# Revit family: BuroSeating_Konfurb Orbit MB_Pedestal
name_source: partatom
category: Furniture
units: mm (PartAtom-declared; Revit-internal decimal feet)

## family parameters
Always vertical = Yes
Cut with Voids When Loaded = No
OmniClass Number = 23.40.70.14.64.11
OmniClass Title = Office Furniture
Room Calculation Point = No
Shared = Yes
Work Plane-Based = No

## types (2) — shared parameters
Assembly Code = E2020
Description = Konfurb Orbi Pedestal Mid Back
Manufacturer = Buro Seating
Model = KON185
NominalDepth = 600 mm
NominalHeight = 835 mm
NominalWidth = 650 mm  [stored 2.13255 ft]
ProductGroup = Orbit
ProductPageURL AU = https://buroseating.com
ProductPageURL NZ = https://buroseating.co.nz
ProductRange = Konfurb
SeatArms = No
SeatBackHeght = 360 mm  [stored 1.1811 ft]
SeatDepth = 470 mm  [stored 1.54199 ft]
SeatHeadRest = No
SeatHeight = 400 mm  [stored 1.31234 ft]
SeatWidth = 515 mm  [stored 1.68963 ft]
Type Comments = Seat Height 435 High
URL = https://buroseating.co.nz
URL AU = https://buroseating.com
WarrantyDescription = Full 5 year guarantee (excluding upholstery)
zero-valued in all types: Default Elevation

## per-type parameters (varying)
| type | BaseFrameMaterial | FeetMaterial | FrameMaterial |
| Buro Elan 159-M3 | <By Category> | <By Category> | <By Category> |
| Konfurb Orbi Pedestal Mid Back | BuroSeating_Metal_Chrome_Semi-Polished | BuroSeating_Steel_Dark Grey | BuroSeating_Steel_Dark Grey |

note: [stored X ft] marks values corroborated as IEEE doubles in the binary element streams (Revit-internal decimal feet)

## geometry (parser evidence)
native form markers: Sweep x5
no freeform markers — native parametric forms only
